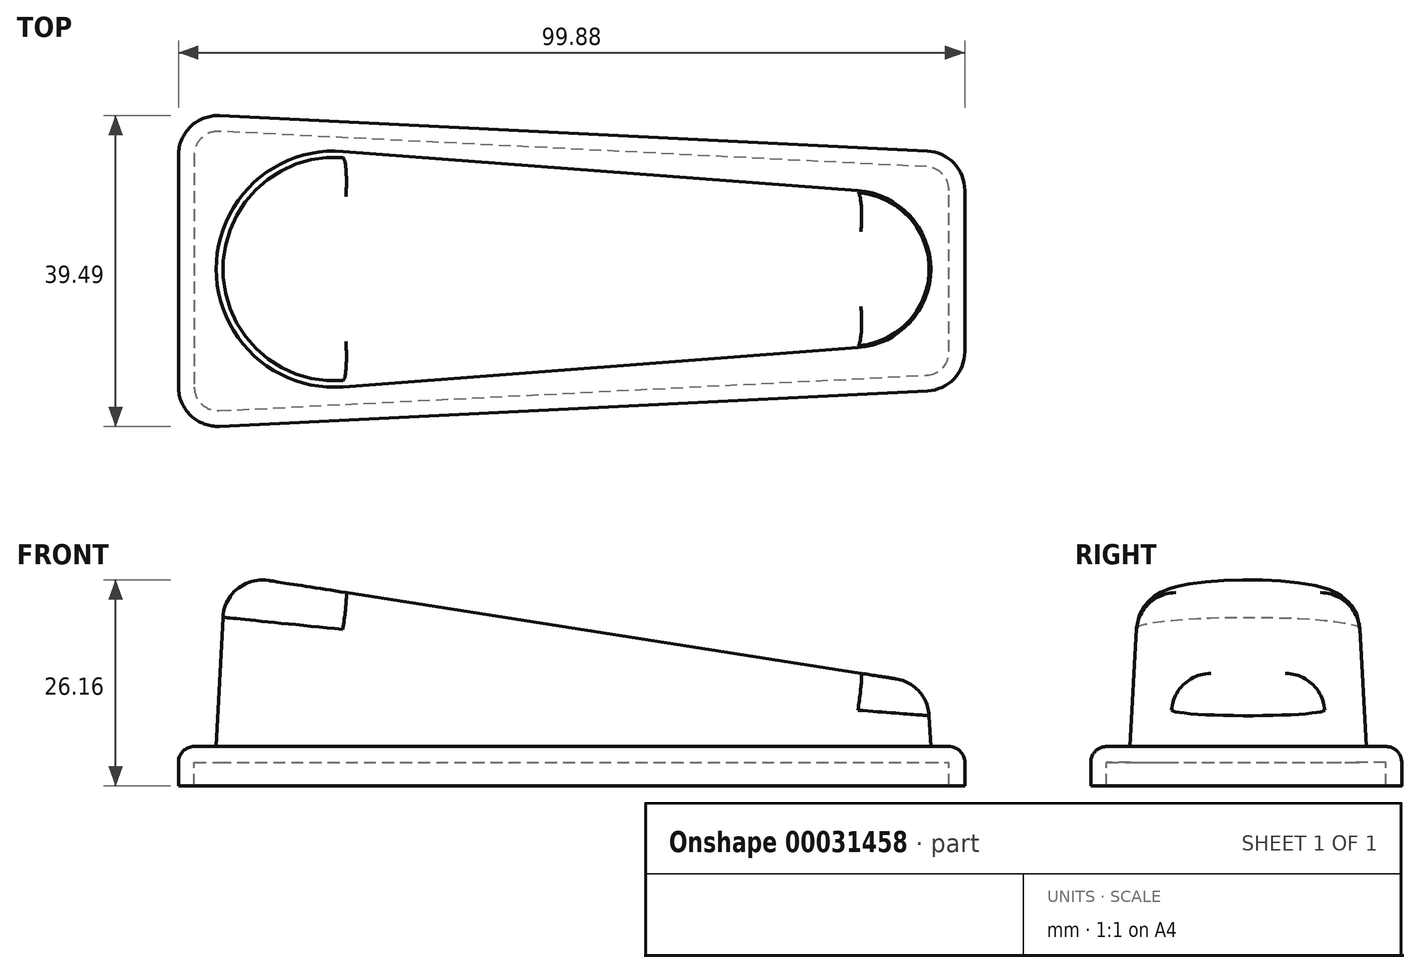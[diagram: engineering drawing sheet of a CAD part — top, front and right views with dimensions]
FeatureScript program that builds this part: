
annotation { "Feature Type Name" : "Feature", "Feature Type Description" : "" }
export const myFeature = defineFeature(function(context is Context, id is Id, definition is map)
    precondition{}
    {
        {
            var Q0;
            Q0=qCreatedBy(makeId("Top.planeOp"),FACE);
            var sketch = newSketch(context, id + "F0", { "sketchPlane" : qUnion([Q0])});
            skLineSegment(sketch, "E0", {"start": v(48.05, 15) * mm, "end": v(-41.83, 19.5) * mm});
            skLineSegment(sketch, "E1", {"start": v(-47.08, 14.5) * mm, "end": v(-47.08, -14.99) * mm});
            skLineSegment(sketch, "E2", {"start": v(-41.83, -19.98) * mm, "end": v(48.05, -15.48) * mm});
            skLineSegment(sketch, "E3", {"start": v(52.8, -10.49) * mm, "end": v(52.8, 10) * mm});
            skPoint(sketch, "E4.visualSharp", {"position": v(-47.08, 19.76) * mm});
            skArc(sketch, "E4.filletArc", {"start": v(-41.83, 19.5) * mm, "mid": v(-45.53, 18.12) * mm, "end": v(-47.08, 14.5) * mm});
            skPoint(sketch, "E5.visualSharp", {"position": v(-47.08, -20.24) * mm});
            skArc(sketch, "E5.filletArc", {"start": v(-47.08, -14.99) * mm, "mid": v(-45.53, -18.6) * mm, "end": v(-41.83, -19.98) * mm});
            skPoint(sketch, "E6.visualSharp", {"position": v(52.8, -15.24) * mm});
            skArc(sketch, "E6.filletArc", {"start": v(48.05, -15.48) * mm, "mid": v(51.42, -13.93) * mm, "end": v(52.8, -10.49) * mm});
            skPoint(sketch, "E7.visualSharp", {"position": v(52.8, 14.76) * mm});
            skArc(sketch, "E7.filletArc", {"start": v(52.8, 10) * mm, "mid": v(51.42, 13.45) * mm, "end": v(48.05, 15) * mm});
            skCircle(sketch, "E8", {"center": v(-27.3, 0) * mm, "radius": 15 * mm});
            skCircle(sketch, "E9", {"center": v(38.48, 0) * mm, "radius": 10 * mm});
            skLineSegment(sketch, "E10", {"start": v(-26.16, 14.96) * mm, "end": v(39.24, 9.97) * mm});
            skLineSegment(sketch, "E11", {"start": v(-26.16, -14.96) * mm, "end": v(39.24, -9.97) * mm});
            skPoint(sketch, "E12", {"position": v(-47.08, -0.24) * mm});
            skPoint(sketch, "E13", {"position": v(52.8, -0.24) * mm});
            skSolve(sketch);
        }
        {
            var Q0;
            Q0=makeQuery(id+"F0.imprint","IMPRINT",FACE,{"disambiguationData":[TD([[makeQuery(id+"F0.imprint","IMPRINT",EDGE,{"derivedFrom":sQuery(id+"F0.wireOp",EDGE,"E0")}),1.0]])]});
            var Q1;
            {var subQ0=sQuery(id+"F0.wireOp",EDGE,"E8");var subQ2=makeQuery(id+"F0.imprint","INTERSECT",VERTEX,{"derivedFrom":[subQ0,sQuery(id+"F0.wireOp",EDGE,"E10")]});Q1=makeQuery(id+"F0.imprint","IMPRINT",FACE,{"disambiguationData":[TD([[makeQuery(id+"F0.imprint","IMPRINT",EDGE,{"disambiguationData":[TD([[subQ2,-1.0]])],"derivedFrom":subQ0}),1.0]])]});}
            var Q2;
            {var subQ1=sQuery(id+"F0.wireOp",EDGE,"E10");Q2=makeQuery(id+"F0.imprint","IMPRINT",FACE,{"disambiguationData":[TD([[makeQuery(id+"F0.imprint","IMPRINT",EDGE,{"derivedFrom":subQ1}),-1.0]])]});}
            var Q3;
            {var subQ0=sQuery(id+"F0.wireOp",EDGE,"E9");var subQ2=makeQuery(id+"F0.imprint","INTERSECT",VERTEX,{"derivedFrom":[subQ0,sQuery(id+"F0.wireOp",EDGE,"E10")]});Q3=makeQuery(id+"F0.imprint","IMPRINT",FACE,{"disambiguationData":[TD([[makeQuery(id+"F0.imprint","IMPRINT",EDGE,{"disambiguationData":[TD([[subQ2,-1.0]])],"derivedFrom":subQ0}),1.0]])]});}
            extrude(context, id + "F1", {"entities" : qUnion([Q0, Q1, Q2, Q3]), "oppositeDirection" : true, "depth" : 5 * mm});
        }
        {
            var Q0;
            {var subQ0=sQuery(id+"F0.wireOp",EDGE,"E9");var subQ2=makeQuery(id+"F0.imprint","INTERSECT",VERTEX,{"derivedFrom":[subQ0,sQuery(id+"F0.wireOp",EDGE,"E10")]});Q0=makeQuery(id+"F0.imprint","IMPRINT",FACE,{"disambiguationData":[TD([[makeQuery(id+"F0.imprint","IMPRINT",EDGE,{"disambiguationData":[TD([[subQ2,-1.0]])],"derivedFrom":subQ0}),1.0]])]});}
            var Q1;
            {var subQ1=sQuery(id+"F0.wireOp",EDGE,"E10");Q1=makeQuery(id+"F0.imprint","IMPRINT",FACE,{"disambiguationData":[TD([[makeQuery(id+"F0.imprint","IMPRINT",EDGE,{"derivedFrom":subQ1}),-1.0]])]});}
            var Q2;
            {var subQ0=sQuery(id+"F0.wireOp",EDGE,"E8");var subQ2=makeQuery(id+"F0.imprint","INTERSECT",VERTEX,{"derivedFrom":[subQ0,sQuery(id+"F0.wireOp",EDGE,"E10")]});Q2=makeQuery(id+"F0.imprint","IMPRINT",FACE,{"disambiguationData":[TD([[makeQuery(id+"F0.imprint","IMPRINT",EDGE,{"disambiguationData":[TD([[subQ2,-1.0]])],"derivedFrom":subQ0}),1.0]])]});}
            extrude(context, id + "F2", {"entities" : qUnion([Q0, Q1, Q2]), "depth" : 25 * mm, "hasDraft" : true, "draftAngle" : 3 * degree, "draftPullDirection" : true});
        }
        {
            var Q0;
            Q0=qCreatedBy(makeId("Front.planeOp"),FACE);
            var sketch = newSketch(context, id + "F3", { "sketchPlane" : qUnion([Q0])});
            skLineSegment(sketch, "E14", {"start": v(-46.8, 22.84) * mm, "end": v(59.1, 6.24) * mm});
            skLineSegment(sketch, "E15", {"start": v(59.1, 6.24) * mm, "end": v(59.1, 33.67) * mm});
            skLineSegment(sketch, "E16", {"start": v(59.1, 33.67) * mm, "end": v(-46.8, 33.67) * mm});
            skLineSegment(sketch, "E17", {"start": v(-46.8, 33.67) * mm, "end": v(-46.8, 22.84) * mm});
            skSolve(sketch);
        }
        {
            var Q0;
            Q0=makeQuery(id+"F3.imprint","IMPRINT",FACE,{"disambiguationData":[TD([[makeQuery(id+"F3.imprint","IMPRINT",EDGE,{"derivedFrom":sQuery(id+"F3.wireOp",EDGE,"E14")}),1.0]])]});
            extrude(context, id + "F4", {"entities" : qUnion([Q0]), "operationType" : NewBodyOperationType.REMOVE, "endBound" : BoundingType.SYMMETRIC, "oppositeDirection" : true, "depth" : 37 * mm});
        }
        {
            var Q0;
            Q0=makeQuery(id+"F1.opExtrude","CAP_EDGE",EDGE,{"disambiguationData":[OSD([sQuery(id+"F0.wireOp",EDGE,"E2")])],"isStart":true});
            fillet(context, id + "F5", {"entities" : qUnion([Q0]), "radius" : 2 * mm, "tangentPropagation" : true, "allowEdgeOverflow" : false});
        }
        {
            var Q0;
            Q0=makeQuery(id+"F4.boolean.opBoolean","INTERSECT",EDGE,{"derivedFrom":[makeQuery(id+"F2.opExtrude","SWEPT_FACE",FACE,{"disambiguationData":[OSD([sQuery(id+"F0.wireOp",EDGE,"E11")])]}),makeQuery(id+"F4.opExtrude","SWEPT_FACE",FACE,{"disambiguationData":[OSD([sQuery(id+"F3.wireOp",EDGE,"E14")])]})]});
            fillet(context, id + "F6", {"entities" : qUnion([Q0]), "radius" : 5 * mm, "tangentPropagation" : true, "allowEdgeOverflow" : false});
        }
        {
            var Q0;
            Q0=makeQuery(id+"F1.opExtrude","CAP_FACE",FACE,{"disambiguationData":[OSD([sQuery(id+"F0.wireOp",EDGE,"E0"),sQuery(id+"F0.wireOp",EDGE,"E1"),sQuery(id+"F0.wireOp",EDGE,"E2"),sQuery(id+"F0.wireOp",EDGE,"E3"),sQuery(id+"F0.wireOp",EDGE,"E4.filletArc"),sQuery(id+"F0.wireOp",EDGE,"E5.filletArc"),sQuery(id+"F0.wireOp",EDGE,"E6.filletArc"),sQuery(id+"F0.wireOp",EDGE,"E7.filletArc")])],"isStart":false});
            shell(context, id + "F7", {"entities" : qUnion([Q0]), "thickness" : 2 * mm});
        }
    });
